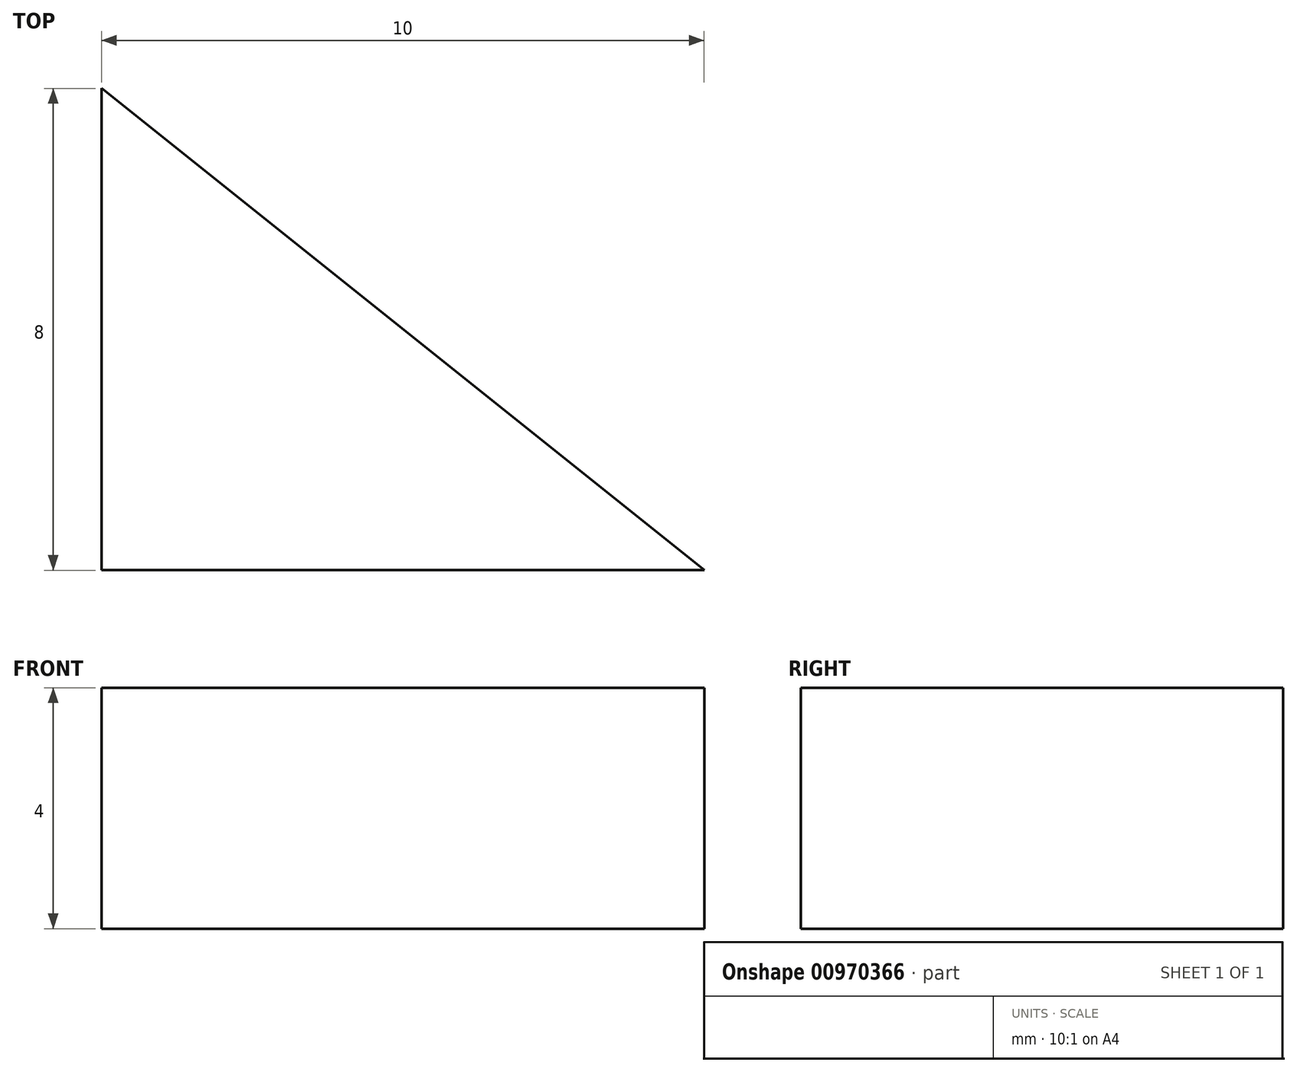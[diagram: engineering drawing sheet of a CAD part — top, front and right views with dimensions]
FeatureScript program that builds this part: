
annotation { "Feature Type Name" : "Feature", "Feature Type Description" : "" }
export const myFeature = defineFeature(function(context is Context, id is Id, definition is map)
    precondition{}
    {
        {
            var Q0;
            Q0=qCreatedBy(makeId("Top.planeOp"),FACE);
            var sketch = newSketch(context, id + "F0", { "sketchPlane" : qUnion([Q0])});
            skLineSegment(sketch, "E0", {"start": v(-3.62, 4.2) * mm, "end": v(-3.62, -3.8) * mm});
            skLineSegment(sketch, "E1", {"start": v(-3.62, -3.8) * mm, "end": v(6.38, -3.8) * mm});
            skLineSegment(sketch, "E2", {"start": v(6.38, -3.8) * mm, "end": v(-3.62, 4.2) * mm});
            skSolve(sketch);
        }
        {
            var Q0;
            Q0=makeQuery(id+"F0.imprint","IMPRINT",FACE,{"disambiguationData":[TD([[makeQuery(id+"F0.imprint","IMPRINT",EDGE,{"derivedFrom":sQuery(id+"F0.wireOp",EDGE,"E0")}),1.0]])]});
            extrude(context, id + "F1", {"entities" : qUnion([Q0]), "oppositeDirection" : true, "depth" : 4 * mm, "offsetDistance" : 25 * mm});
        }
    });
